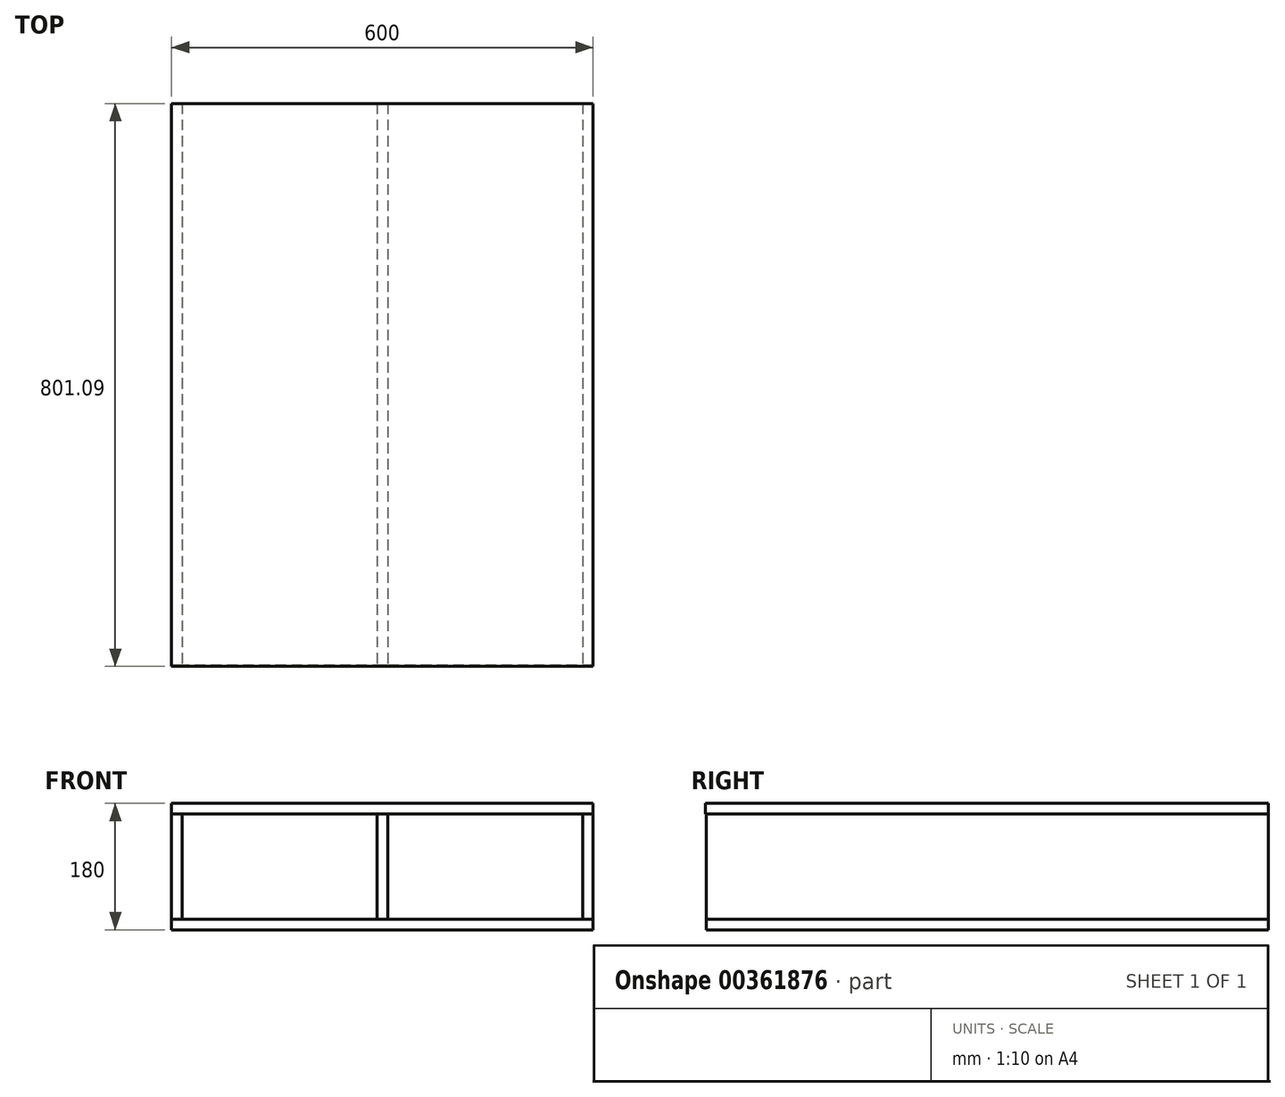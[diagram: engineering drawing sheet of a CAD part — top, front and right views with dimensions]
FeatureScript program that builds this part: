
annotation { "Feature Type Name" : "Feature", "Feature Type Description" : "" }
export const myFeature = defineFeature(function(context is Context, id is Id, definition is map)
    precondition{}
    {
        {
            var Q0;
            Q0=qCreatedBy(makeId("Top.planeOp"),FACE);
            var sketch = newSketch(context, id + "F0", { "sketchPlane" : qUnion([Q0])});
            skLineSegment(sketch, "E0.bottom", {"start": v(0, 0) * mm, "end": v(-300, 0) * mm});
            skLineSegment(sketch, "E0.top", {"start": v(0, 400) * mm, "end": v(-300, 400) * mm});
            skLineSegment(sketch, "E0.left", {"start": v(0, 0) * mm, "end": v(0, 400) * mm});
            skLineSegment(sketch, "E0.right", {"start": v(-300, 0) * mm, "end": v(-300, 400) * mm});
            skLineSegment(sketch, "E1.MirrorCS", {"start": v(300, 0) * mm, "end": v(300, 400) * mm});
            skLineSegment(sketch, "E2.MirrorCS", {"start": v(0, 400) * mm, "end": v(300, 400) * mm});
            skLineSegment(sketch, "E3.MirrorCS", {"start": v(0, 0) * mm, "end": v(300, 0) * mm});
            skLineSegment(sketch, "E4.MirrorCS", {"start": v(0, 0) * mm, "end": v(0, -400) * mm});
            skLineSegment(sketch, "E5.MirrorCS", {"start": v(300, 0) * mm, "end": v(300, -400) * mm});
            skLineSegment(sketch, "E6.MirrorCS", {"start": v(0, -400) * mm, "end": v(300, -400) * mm});
            skLineSegment(sketch, "E7.MirrorCS", {"start": v(-300, 0) * mm, "end": v(-300, -400) * mm});
            skLineSegment(sketch, "E8.MirrorCS", {"start": v(0, -400) * mm, "end": v(-300, -400) * mm});
            skSolve(sketch);
        }
        {
            var Q0;
            Q0=makeQuery(id+"F0.imprint","IMPRINT",FACE,{"disambiguationData":[TD([[makeQuery(id+"F0.imprint","IMPRINT",EDGE,{"derivedFrom":sQuery(id+"F0.wireOp",EDGE,"E0.bottom")}),1.0]])]});
            var Q1;
            Q1=makeQuery(id+"F0.imprint","IMPRINT",FACE,{"disambiguationData":[TD([[makeQuery(id+"F0.imprint","IMPRINT",EDGE,{"derivedFrom":sQuery(id+"F0.wireOp",EDGE,"E5.MirrorCS")}),-1.0]])]});
            var Q2;
            Q2=makeQuery(id+"F0.imprint","IMPRINT",FACE,{"disambiguationData":[TD([[makeQuery(id+"F0.imprint","IMPRINT",EDGE,{"derivedFrom":sQuery(id+"F0.wireOp",EDGE,"E0.left")}),-1.0]])]});
            var Q3;
            Q3=makeQuery(id+"F0.imprint","IMPRINT",FACE,{"disambiguationData":[TD([[makeQuery(id+"F0.imprint","IMPRINT",EDGE,{"derivedFrom":sQuery(id+"F0.wireOp",EDGE,"E0.top")}),1.0]])]});
            extrude(context, id + "F1", {"entities" : qUnion([Q0, Q1, Q2, Q3]), "depth" : 15 * mm});
        }
        {
            var Q0;
            Q0=makeQuery(id+"F1.opExtrude","CAP_FACE",FACE,{"disambiguationData":[OSD([sQuery(id+"F0.wireOp",EDGE,"E0.top"),sQuery(id+"F0.wireOp",EDGE,"E0.right"),sQuery(id+"F0.wireOp",EDGE,"E2.MirrorCS"),sQuery(id+"F0.wireOp",EDGE,"E1.MirrorCS"),sQuery(id+"F0.wireOp",EDGE,"E5.MirrorCS"),sQuery(id+"F0.wireOp",EDGE,"E6.MirrorCS"),sQuery(id+"F0.wireOp",EDGE,"E7.MirrorCS"),sQuery(id+"F0.wireOp",EDGE,"E8.MirrorCS")])],"isStart":false});
            var sketch = newSketch(context, id + "F2", { "sketchPlane" : qUnion([Q0])});
            skLineSegment(sketch, "E9.bottom", {"start": v(-300, 400) * mm, "end": v(-285, 400) * mm});
            skLineSegment(sketch, "E9.top", {"start": v(-300, -400) * mm, "end": v(-285, -400) * mm});
            skLineSegment(sketch, "E9.left", {"start": v(-300, 400) * mm, "end": v(-300, -400) * mm});
            skLineSegment(sketch, "E9.right", {"start": v(-285, 400) * mm, "end": v(-285, -400) * mm});
            skSolve(sketch);
        }
        {
            var Q0;
            Q0=makeQuery(id+"F2.imprint","IMPRINT",FACE,{"disambiguationData":[TD([[makeQuery(id+"F2.imprint","IMPRINT",EDGE,{"derivedFrom":sQuery(id+"F2.wireOp",EDGE,"E9.bottom")}),-1.0]])]});
            extrude(context, id + "F3", {"entities" : qUnion([Q0]), "depth" : 150 * mm});
        }
        {
            var Q0;
            Q0=makeQuery(id+"F3.opExtrude","SWEPT_BODY",BODY,{"disambiguationData":[OSD([sQuery(id+"F2.wireOp",EDGE,"E9.bottom"),sQuery(id+"F2.wireOp",EDGE,"E9.top"),sQuery(id+"F2.wireOp",EDGE,"E9.left"),sQuery(id+"F2.wireOp",EDGE,"E9.right")])]});
            var Q1;
            Q1=qCreatedBy(makeId("Right.planeOp"),FACE);
            mirror(context, id + "F4", {"entities" : qUnion([Q0]), "mirrorPlane" : qUnion([Q1])});
        }
        {
            var Q0;
            Q0=makeQuery(id+"F1.opExtrude","CAP_FACE",FACE,{"disambiguationData":[OSD([sQuery(id+"F0.wireOp",EDGE,"E0.top"),sQuery(id+"F0.wireOp",EDGE,"E0.right"),sQuery(id+"F0.wireOp",EDGE,"E2.MirrorCS"),sQuery(id+"F0.wireOp",EDGE,"E1.MirrorCS"),sQuery(id+"F0.wireOp",EDGE,"E5.MirrorCS"),sQuery(id+"F0.wireOp",EDGE,"E6.MirrorCS"),sQuery(id+"F0.wireOp",EDGE,"E7.MirrorCS"),sQuery(id+"F0.wireOp",EDGE,"E8.MirrorCS")])],"isStart":false});
            var sketch = newSketch(context, id + "F5", { "sketchPlane" : qUnion([Q0])});
            skLineSegment(sketch, "E10.bottom", {"start": v(0, 400) * mm, "end": v(-7.5, 400) * mm});
            skLineSegment(sketch, "E10.top", {"start": v(0, -400) * mm, "end": v(-7.5, -400) * mm});
            skLineSegment(sketch, "E10.left", {"start": v(0, 400) * mm, "end": v(0, -400) * mm});
            skLineSegment(sketch, "E10.right", {"start": v(-7.5, 400) * mm, "end": v(-7.5, -400) * mm});
            skLineSegment(sketch, "E11.MirrorCS", {"start": v(0, -400) * mm, "end": v(7.5, -400) * mm});
            skLineSegment(sketch, "E12.MirrorCS", {"start": v(0, 400) * mm, "end": v(7.5, 400) * mm});
            skLineSegment(sketch, "E13.MirrorCS", {"start": v(7.5, 400) * mm, "end": v(7.5, -400) * mm});
            skSolve(sketch);
        }
        {
            var Q0;
            Q0=makeQuery(id+"F5.imprint","IMPRINT",FACE,{"disambiguationData":[TD([[makeQuery(id+"F5.imprint","IMPRINT",EDGE,{"derivedFrom":sQuery(id+"F5.wireOp",EDGE,"E11.MirrorCS")}),-1.0]])]});
            var Q1;
            Q1=makeQuery(id+"F5.imprint","IMPRINT",FACE,{"disambiguationData":[TD([[makeQuery(id+"F5.imprint","IMPRINT",EDGE,{"derivedFrom":sQuery(id+"F5.wireOp",EDGE,"E10.bottom")}),-1.0]])]});
            extrude(context, id + "F6", {"entities" : qUnion([Q0, Q1]), "depth" : 150 * mm});
        }
        {
            var Q0;
            Q0=makeQuery(id+"F3.opExtrude","CAP_FACE",FACE,{"disambiguationData":[OSD([sQuery(id+"F2.wireOp",EDGE,"E9.bottom"),sQuery(id+"F2.wireOp",EDGE,"E9.top"),sQuery(id+"F2.wireOp",EDGE,"E9.left"),sQuery(id+"F2.wireOp",EDGE,"E9.right")])],"isStart":false});
            var sketch = newSketch(context, id + "F7", { "sketchPlane" : qUnion([Q0])});
            skLineSegment(sketch, "E14.bottom", {"start": v(-300, 400) * mm, "end": v(300, 400) * mm});
            skLineSegment(sketch, "E14.top", {"start": v(-300, -401.1) * mm, "end": v(300, -401.1) * mm});
            skLineSegment(sketch, "E14.left", {"start": v(-300, 400) * mm, "end": v(-300, -401.1) * mm});
            skLineSegment(sketch, "E14.right", {"start": v(300, 400) * mm, "end": v(300, -401.1) * mm});
            skSolve(sketch);
        }
        {
            var Q0;
            {var subQ3=sQuery(id+"F7.wireOp",EDGE,"E14.top");Q0=makeQuery(id+"F7.imprint","IMPRINT",FACE,{"disambiguationData":[TD([[makeQuery(id+"F7.imprint","IMPRINT",EDGE,{"derivedFrom":subQ3}),1.0]])]});}
            var Q1;
            {var subQ4=makeQuery(id+"F3.opExtrude","CAP_EDGE",EDGE,{"disambiguationData":[OSD([sQuery(id+"F2.wireOp",EDGE,"E9.top")])],"isStart":false});Q1=makeQuery(id+"F7.imprint","IMPRINT",FACE,{"disambiguationData":[TD([[makeQuery(id+"F7.imprint","IMPRINT",EDGE,{"derivedFrom":subQ4}),-1.0]])]});}
            var Q2;
            Q2=sQuery(id+"F7.wireOp",EDGE,"E14.bottom");
            var Q3;
            Q3=sQuery(id+"F7.wireOp",EDGE,"E14.left");
            var Q4;
            Q4=sQuery(id+"F7.wireOp",EDGE,"E14.top");
            var Q5;
            Q5=sQuery(id+"F7.wireOp",EDGE,"E14.right");
            extrude(context, id + "F8", {"entities" : qUnion([Q0, Q1]), "surfaceEntities" : qUnion([Q2, Q3, Q4, Q5]), "depth" : 15 * mm});
        }
    });
